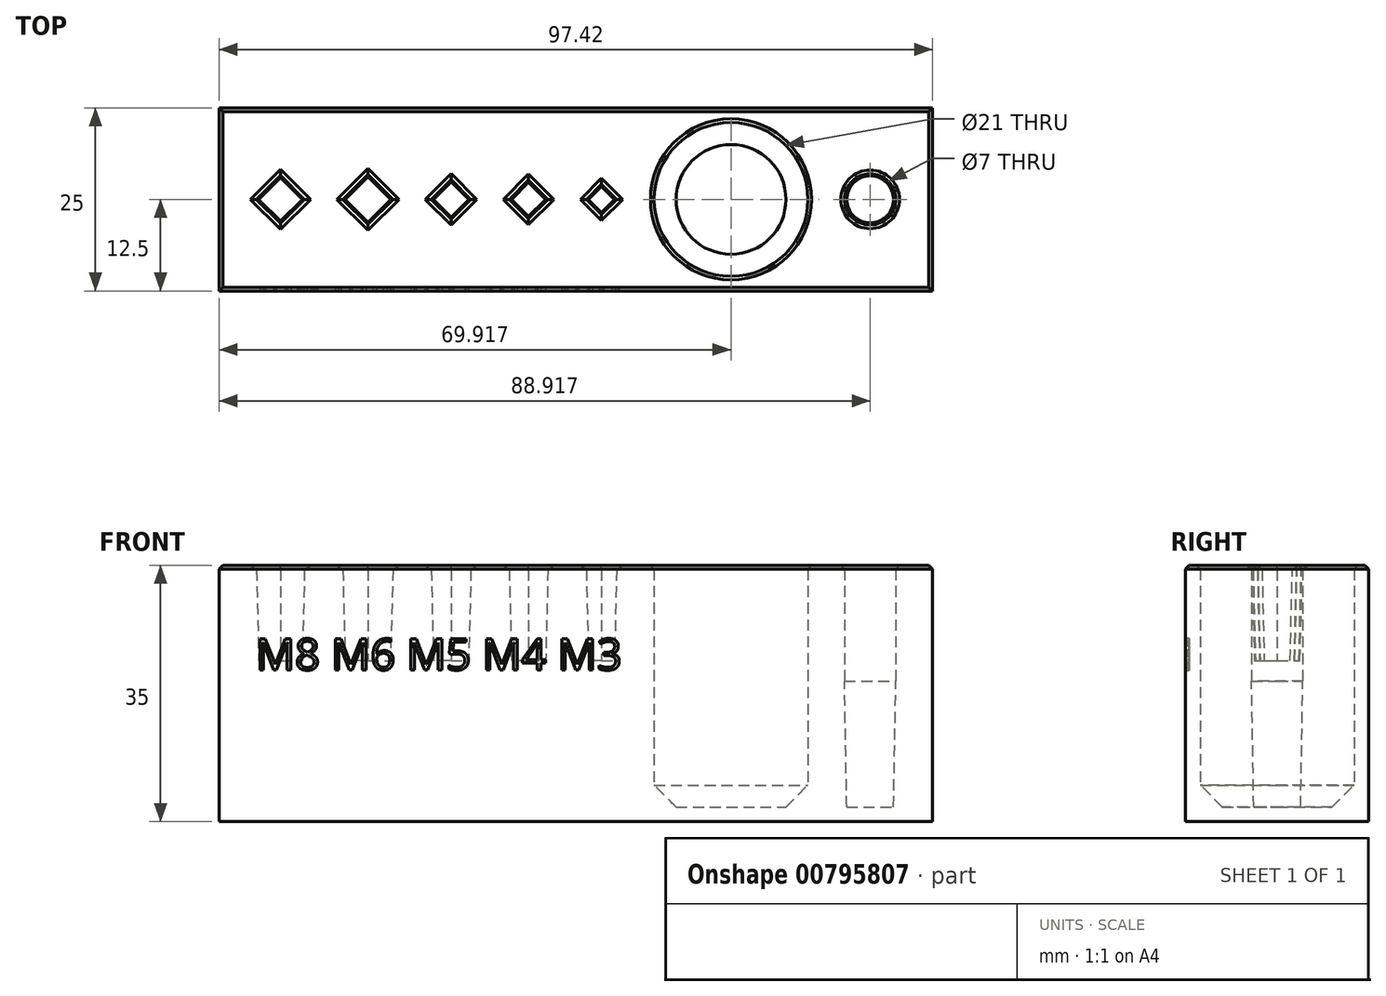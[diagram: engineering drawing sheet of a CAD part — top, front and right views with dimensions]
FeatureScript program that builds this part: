
annotation { "Feature Type Name" : "Feature", "Feature Type Description" : "" }
export const myFeature = defineFeature(function(context is Context, id is Id, definition is map)
    precondition{}
    {
        {
            var Q0;
            Q0=qCreatedBy(makeId("Top.planeOp"),FACE);
            var sketch = newSketch(context, id + "F0", { "sketchPlane" : qUnion([Q0])});
            skLineSegment(sketch, "E0.bottom", {"start": v(-10.63, 12.5) * mm, "end": v(86.79, 12.5) * mm});
            skLineSegment(sketch, "E0.top", {"start": v(-10.63, -12.5) * mm, "end": v(86.79, -12.5) * mm});
            skLineSegment(sketch, "E0.left", {"start": v(-10.63, 12.5) * mm, "end": v(-10.63, -12.5) * mm});
            skLineSegment(sketch, "E0.right", {"start": v(86.79, 12.5) * mm, "end": v(86.79, -12.5) * mm});
            skLineSegment(sketch, "E1", {"start": v(-71.8, 0) * mm, "end": v(104.16, 0) * mm, "construction": true});
            skCircle(sketch, "E2", {"center": v(59.29, 0) * mm, "radius": 10.5 * mm});
            skLineSegment(sketch, "E3", {"start": v(-2.23, 3.4) * mm, "end": v(-5.63, 0) * mm});
            skLineSegment(sketch, "E4", {"start": v(-5.63, 0) * mm, "end": v(-2.23, -3.4) * mm});
            skLineSegment(sketch, "E5", {"start": v(-2.23, -3.4) * mm, "end": v(1.16, 0) * mm});
            skLineSegment(sketch, "E6", {"start": v(1.16, 0) * mm, "end": v(-2.23, 3.4) * mm});
            skLineSegment(sketch, "E7", {"start": v(9.7, 3.54) * mm, "end": v(6.16, 0) * mm});
            skLineSegment(sketch, "E8", {"start": v(6.16, 0) * mm, "end": v(9.7, -3.54) * mm});
            skLineSegment(sketch, "E9", {"start": v(9.7, -3.54) * mm, "end": v(13.23, 0) * mm});
            skLineSegment(sketch, "E10", {"start": v(13.23, 0) * mm, "end": v(9.7, 3.54) * mm});
            skLineSegment(sketch, "E11", {"start": v(21.06, 2.83) * mm, "end": v(18.23, 0) * mm});
            skLineSegment(sketch, "E12", {"start": v(18.23, 0) * mm, "end": v(21.06, -2.83) * mm});
            skLineSegment(sketch, "E13", {"start": v(21.06, -2.83) * mm, "end": v(23.89, 0) * mm});
            skLineSegment(sketch, "E14", {"start": v(23.89, 0) * mm, "end": v(21.06, 2.83) * mm});
            skLineSegment(sketch, "E15", {"start": v(31.65, 2.76) * mm, "end": v(28.89, 0) * mm});
            skLineSegment(sketch, "E16", {"start": v(28.89, 0) * mm, "end": v(31.65, -2.76) * mm});
            skLineSegment(sketch, "E17", {"start": v(31.65, -2.76) * mm, "end": v(34.4, 0) * mm});
            skLineSegment(sketch, "E18", {"start": v(34.4, 0) * mm, "end": v(31.65, 2.76) * mm});
            skLineSegment(sketch, "E19", {"start": v(41.6, 2.2) * mm, "end": v(39.4, 0) * mm});
            skLineSegment(sketch, "E20", {"start": v(39.4, 0) * mm, "end": v(41.6, -2.2) * mm});
            skLineSegment(sketch, "E21", {"start": v(41.6, -2.2) * mm, "end": v(43.79, 0) * mm});
            skLineSegment(sketch, "E22", {"start": v(43.79, 0) * mm, "end": v(41.6, 2.2) * mm});
            skCircle(sketch, "E23", {"center": v(78.29, 0) * mm, "radius": 3.5 * mm});
            skSolve(sketch);
        }
        {
            var Q0;
            Q0=makeQuery(id+"F0.imprint","IMPRINT",FACE,{"disambiguationData":[TD([[makeQuery(id+"F0.imprint","IMPRINT",EDGE,{"derivedFrom":sQuery(id+"F0.wireOp",EDGE,"E0.bottom")}),-1.0]])]});
            extrude(context, id + "F1", {"entities" : qUnion([Q0]), "depth" : 13 * mm, "offsetDistance" : 25 * mm});
        }
        {
            var Q0;
            Q0=makeQuery(id+"F1.opExtrude","CAP_FACE",FACE,{"disambiguationData":[OSD([sQuery(id+"F0.wireOp",EDGE,"E0.bottom"),sQuery(id+"F0.wireOp",EDGE,"E0.top"),sQuery(id+"F0.wireOp",EDGE,"E0.left"),sQuery(id+"F0.wireOp",EDGE,"E0.right"),sQuery(id+"F0.wireOp",EDGE,"E2"),sQuery(id+"F0.wireOp",EDGE,"E3"),sQuery(id+"F0.wireOp",EDGE,"E4"),sQuery(id+"F0.wireOp",EDGE,"E5"),sQuery(id+"F0.wireOp",EDGE,"E6"),sQuery(id+"F0.wireOp",EDGE,"E7"),sQuery(id+"F0.wireOp",EDGE,"E8"),sQuery(id+"F0.wireOp",EDGE,"E9"),sQuery(id+"F0.wireOp",EDGE,"E10"),sQuery(id+"F0.wireOp",EDGE,"E11"),sQuery(id+"F0.wireOp",EDGE,"E12"),sQuery(id+"F0.wireOp",EDGE,"E13"),sQuery(id+"F0.wireOp",EDGE,"E14"),sQuery(id+"F0.wireOp",EDGE,"E15"),sQuery(id+"F0.wireOp",EDGE,"E16"),sQuery(id+"F0.wireOp",EDGE,"E17"),sQuery(id+"F0.wireOp",EDGE,"E18"),sQuery(id+"F0.wireOp",EDGE,"E19"),sQuery(id+"F0.wireOp",EDGE,"E20"),sQuery(id+"F0.wireOp",EDGE,"E21"),sQuery(id+"F0.wireOp",EDGE,"E22")])],"isStart":true});
            var sketch = newSketch(context, id + "F2", { "sketchPlane" : qUnion([Q0])});
            skLineSegment(sketch, "E24.bottom", {"start": v(-10.63, 12.5) * mm, "end": v(86.79, 12.5) * mm});
            skLineSegment(sketch, "E24.top", {"start": v(-10.63, -12.5) * mm, "end": v(86.79, -12.5) * mm});
            skLineSegment(sketch, "E24.left", {"start": v(-10.63, 12.5) * mm, "end": v(-10.63, -12.5) * mm});
            skLineSegment(sketch, "E24.right", {"start": v(86.79, 12.5) * mm, "end": v(86.79, -12.5) * mm});
            skCircle(sketch, "E25", {"center": v(59.29, 0) * mm, "radius": 10.5 * mm});
            skSolve(sketch);
        }
        {
            var Q0;
            Q0=makeQuery(id+"F2.imprint","IMPRINT",FACE,{"disambiguationData":[TD([[makeQuery(id+"F2.imprint","IMPRINT",EDGE,{"derivedFrom":makeQuery(id+"F1.opExtrude","CAP_EDGE",EDGE,{"disambiguationData":[OSD([sQuery(id+"F0.wireOp",EDGE,"E3")])],"isStart":true})}),-1.0]])]});
            var Q1;
            Q1=makeQuery(id+"F2.imprint","IMPRINT",FACE,{"disambiguationData":[TD([[makeQuery(id+"F2.imprint","IMPRINT",EDGE,{"derivedFrom":makeQuery(id+"F1.opExtrude","CAP_EDGE",EDGE,{"disambiguationData":[OSD([sQuery(id+"F0.wireOp",EDGE,"E7")])],"isStart":true})}),-1.0]])]});
            var Q2;
            Q2=makeQuery(id+"F2.imprint","IMPRINT",FACE,{"disambiguationData":[TD([[makeQuery(id+"F2.imprint","IMPRINT",EDGE,{"derivedFrom":makeQuery(id+"F1.opExtrude","CAP_EDGE",EDGE,{"disambiguationData":[OSD([sQuery(id+"F0.wireOp",EDGE,"E11")])],"isStart":true})}),-1.0]])]});
            var Q3;
            Q3=makeQuery(id+"F2.imprint","IMPRINT",FACE,{"disambiguationData":[TD([[makeQuery(id+"F2.imprint","IMPRINT",EDGE,{"derivedFrom":makeQuery(id+"F1.opExtrude","CAP_EDGE",EDGE,{"disambiguationData":[OSD([sQuery(id+"F0.wireOp",EDGE,"E15")])],"isStart":true})}),-1.0]])]});
            var Q4;
            Q4=makeQuery(id+"F2.imprint","IMPRINT",FACE,{"disambiguationData":[TD([[makeQuery(id+"F2.imprint","IMPRINT",EDGE,{"derivedFrom":makeQuery(id+"F1.opExtrude","CAP_EDGE",EDGE,{"disambiguationData":[OSD([sQuery(id+"F0.wireOp",EDGE,"E19")])],"isStart":true})}),-1.0]])]});
            var Q5;
            Q5=makeQuery(id+"F2.imprint","IMPRINT",FACE,{"disambiguationData":[TD([[makeQuery(id+"F2.imprint","IMPRINT",EDGE,{"derivedFrom":sQuery(id+"F2.wireOp",EDGE,"E24.bottom")}),-1.0]])]});
            extrude(context, id + "F3", {"entities" : qUnion([Q0, Q1, Q2, Q3, Q4, Q5]), "operationType" : NewBodyOperationType.ADD, "depth" : 20 * mm, "offsetDistance" : 25 * mm});
        }
        {
            var Q0;
            Q0=makeQuery(id+"F1.opExtrude","CAP_FACE",FACE,{"disambiguationData":[OSD([sQuery(id+"F0.wireOp",EDGE,"E0.bottom"),sQuery(id+"F0.wireOp",EDGE,"E0.top"),sQuery(id+"F0.wireOp",EDGE,"E0.left"),sQuery(id+"F0.wireOp",EDGE,"E0.right"),sQuery(id+"F0.wireOp",EDGE,"E2"),sQuery(id+"F0.wireOp",EDGE,"E3"),sQuery(id+"F0.wireOp",EDGE,"E4"),sQuery(id+"F0.wireOp",EDGE,"E5"),sQuery(id+"F0.wireOp",EDGE,"E6"),sQuery(id+"F0.wireOp",EDGE,"E7"),sQuery(id+"F0.wireOp",EDGE,"E8"),sQuery(id+"F0.wireOp",EDGE,"E9"),sQuery(id+"F0.wireOp",EDGE,"E10"),sQuery(id+"F0.wireOp",EDGE,"E11"),sQuery(id+"F0.wireOp",EDGE,"E12"),sQuery(id+"F0.wireOp",EDGE,"E13"),sQuery(id+"F0.wireOp",EDGE,"E14"),sQuery(id+"F0.wireOp",EDGE,"E15"),sQuery(id+"F0.wireOp",EDGE,"E16"),sQuery(id+"F0.wireOp",EDGE,"E17"),sQuery(id+"F0.wireOp",EDGE,"E18"),sQuery(id+"F0.wireOp",EDGE,"E19"),sQuery(id+"F0.wireOp",EDGE,"E20"),sQuery(id+"F0.wireOp",EDGE,"E21"),sQuery(id+"F0.wireOp",EDGE,"E22")])],"isStart":false});
            chamfer(context, id + "F4", {"entities" : qUnion([Q0]), "width" : 0.5 * mm, "tangentPropagation" : true});
        }
        {
            var Q0;
            Q0=makeQuery(id+"F3.opExtrude","CAP_FACE",FACE,{"disambiguationData":[OSD([sQuery(id+"F2.wireOp",EDGE,"E24.bottom"),sQuery(id+"F2.wireOp",EDGE,"E24.top"),sQuery(id+"F2.wireOp",EDGE,"E24.left"),sQuery(id+"F2.wireOp",EDGE,"E24.right"),sQuery(id+"F2.wireOp",EDGE,"E25")])],"isStart":false});
            var sketch = newSketch(context, id + "F5", { "sketchPlane" : qUnion([Q0])});
            skLineSegment(sketch, "E26.bottom", {"start": v(-10.63, 12.5) * mm, "end": v(86.79, 12.5) * mm});
            skLineSegment(sketch, "E26.top", {"start": v(-10.63, -12.5) * mm, "end": v(86.79, -12.5) * mm});
            skLineSegment(sketch, "E26.left", {"start": v(-10.63, 12.5) * mm, "end": v(-10.63, -12.5) * mm});
            skLineSegment(sketch, "E26.right", {"start": v(86.79, 12.5) * mm, "end": v(86.79, -12.5) * mm});
            skSolve(sketch);
        }
        {
            var Q0;
            Q0 = qSketchRegion(id + "F5", true);
            extrude(context, id + "F6", {"entities" : qUnion([Q0]), "operationType" : NewBodyOperationType.ADD, "depth" : 2 * mm, "offsetDistance" : 25 * mm});
        }
        {
            var Q0;
            Q0=makeQuery(id+"F6.boolean.opBoolean","SPLIT",FACE,{"disambiguationData":[TD([makeQuery(id+"F1.opExtrude","SWEPT_FACE",FACE,{"disambiguationData":[OSD([sQuery(id+"F0.wireOp",EDGE,"E2")])]})])],"derivedFrom":makeQuery(id+"F6.opExtrude","CAP_FACE",FACE,{"disambiguationData":[OSD([sQuery(id+"F5.wireOp",EDGE,"E26.bottom"),sQuery(id+"F5.wireOp",EDGE,"E26.top"),sQuery(id+"F5.wireOp",EDGE,"E26.left"),sQuery(id+"F5.wireOp",EDGE,"E26.right")])],"isStart":true})});
            chamfer(context, id + "F7", {"entities" : qUnion([Q0]), "width" : 3 * mm, "tangentPropagation" : true});
        }
        {
            var Q0;
            Q0=makeQuery(id+"F3.boolean.opBoolean","SPLIT",FACE,{"disambiguationData":[TD([makeQuery(id+"F1.opExtrude","SWEPT_FACE",FACE,{"disambiguationData":[OSD([sQuery(id+"F0.wireOp",EDGE,"E7")])]})])],"derivedFrom":makeQuery(id+"F3.opExtrude","CAP_FACE",FACE,{"disambiguationData":[OSD([sQuery(id+"F2.wireOp",EDGE,"E24.bottom"),sQuery(id+"F2.wireOp",EDGE,"E24.top"),sQuery(id+"F2.wireOp",EDGE,"E24.left"),sQuery(id+"F2.wireOp",EDGE,"E24.right"),sQuery(id+"F2.wireOp",EDGE,"E25")])],"isStart":true})});
            var Q1;
            Q1=makeQuery(id+"F3.boolean.opBoolean","SPLIT",FACE,{"disambiguationData":[TD([makeQuery(id+"F1.opExtrude","SWEPT_FACE",FACE,{"disambiguationData":[OSD([sQuery(id+"F0.wireOp",EDGE,"E11")])]})])],"derivedFrom":makeQuery(id+"F3.opExtrude","CAP_FACE",FACE,{"disambiguationData":[OSD([sQuery(id+"F2.wireOp",EDGE,"E24.bottom"),sQuery(id+"F2.wireOp",EDGE,"E24.top"),sQuery(id+"F2.wireOp",EDGE,"E24.left"),sQuery(id+"F2.wireOp",EDGE,"E24.right"),sQuery(id+"F2.wireOp",EDGE,"E25")])],"isStart":true})});
            var Q2;
            Q2=makeQuery(id+"F3.boolean.opBoolean","SPLIT",FACE,{"disambiguationData":[TD([makeQuery(id+"F1.opExtrude","SWEPT_FACE",FACE,{"disambiguationData":[OSD([sQuery(id+"F0.wireOp",EDGE,"E15")])]})])],"derivedFrom":makeQuery(id+"F3.opExtrude","CAP_FACE",FACE,{"disambiguationData":[OSD([sQuery(id+"F2.wireOp",EDGE,"E24.bottom"),sQuery(id+"F2.wireOp",EDGE,"E24.top"),sQuery(id+"F2.wireOp",EDGE,"E24.left"),sQuery(id+"F2.wireOp",EDGE,"E24.right"),sQuery(id+"F2.wireOp",EDGE,"E25")])],"isStart":true})});
            var Q3;
            Q3=makeQuery(id+"F3.boolean.opBoolean","SPLIT",FACE,{"disambiguationData":[TD([makeQuery(id+"F1.opExtrude","SWEPT_FACE",FACE,{"disambiguationData":[OSD([sQuery(id+"F0.wireOp",EDGE,"E19")])]})])],"derivedFrom":makeQuery(id+"F3.opExtrude","CAP_FACE",FACE,{"disambiguationData":[OSD([sQuery(id+"F2.wireOp",EDGE,"E24.bottom"),sQuery(id+"F2.wireOp",EDGE,"E24.top"),sQuery(id+"F2.wireOp",EDGE,"E24.left"),sQuery(id+"F2.wireOp",EDGE,"E24.right"),sQuery(id+"F2.wireOp",EDGE,"E25")])],"isStart":true})});
            var Q4;
            Q4=makeQuery(id+"F3.boolean.opBoolean","SPLIT",FACE,{"disambiguationData":[TD([makeQuery(id+"F1.opExtrude","SWEPT_FACE",FACE,{"disambiguationData":[OSD([sQuery(id+"F0.wireOp",EDGE,"E3")])]})])],"derivedFrom":makeQuery(id+"F3.opExtrude","CAP_FACE",FACE,{"disambiguationData":[OSD([sQuery(id+"F2.wireOp",EDGE,"E24.bottom"),sQuery(id+"F2.wireOp",EDGE,"E24.top"),sQuery(id+"F2.wireOp",EDGE,"E24.left"),sQuery(id+"F2.wireOp",EDGE,"E24.right"),sQuery(id+"F2.wireOp",EDGE,"E25")])],"isStart":true})});
            var Q5;
            {var subQ0=sQuery(id+"F0.wireOp",EDGE,"E23");Q5=makeQuery(id+"F6.boolean.opBoolean","SPLIT",FACE,{"disambiguationData":[TD([makeQuery(id+"F1.opExtrude","SWEPT_FACE",FACE,{"disambiguationData":[OSD([subQ0])]})])],"derivedFrom":makeQuery(id+"F6.opExtrude","CAP_FACE",FACE,{"disambiguationData":[OSD([sQuery(id+"F5.wireOp",EDGE,"E26.bottom"),sQuery(id+"F5.wireOp",EDGE,"E26.top"),sQuery(id+"F5.wireOp",EDGE,"E26.left"),sQuery(id+"F5.wireOp",EDGE,"E26.right")])],"isStart":true})});}
            chamfer(context, id + "F8", {"entities" : qUnion([Q0, Q1, Q2, Q3, Q4, Q5]), "chamferType" : ChamferType.OFFSET_ANGLE, "width" : 0.3 * mm, "oppositeDirection" : false, "angle" : 89 * degree, "tangentPropagation" : true});
        }
        {
            var Q0;
            Q0=makeQuery(id+"F6.boolean.opBoolean","MERGE",FACE,{"derivedFrom":[makeQuery(id+"F3.boolean.opBoolean","MERGE",FACE,{"derivedFrom":[makeQuery(id+"F1.opExtrude","SWEPT_FACE",FACE,{"disambiguationData":[OSD([sQuery(id+"F0.wireOp",EDGE,"E0.top")])]}),makeQuery(id+"F3.opExtrude","SWEPT_FACE",FACE,{"disambiguationData":[OSD([sQuery(id+"F2.wireOp",EDGE,"E24.bottom")])]})]}),makeQuery(id+"F6.opExtrude","SWEPT_FACE",FACE,{"disambiguationData":[OSD([sQuery(id+"F5.wireOp",EDGE,"E26.bottom")])]})]});
            var sketch = newSketch(context, id + "F9", { "sketchPlane" : qUnion([Q0])});
            skText(sketch, "E27", { "text": "M8 M6 M5 M4 M3\n", "fontName": "OpenSans-Regular.ttf"});
            const initialGuessF9  = {"E27": [-0.00563, -0.00128, 1, 0, 0.00428]};
            skSetInitialGuess(sketch, initialGuessF9);
            skSolve(sketch);
        }
        {
            var Q0;
            Q0 = qSketchRegion(id + "F9", true);
            extrude(context, id + "F10", {"entities" : qUnion([Q0]), "operationType" : NewBodyOperationType.REMOVE, "oppositeDirection" : true, "depth" : 0.5 * mm, "offsetDistance" : 25 * mm});
        }
    });
